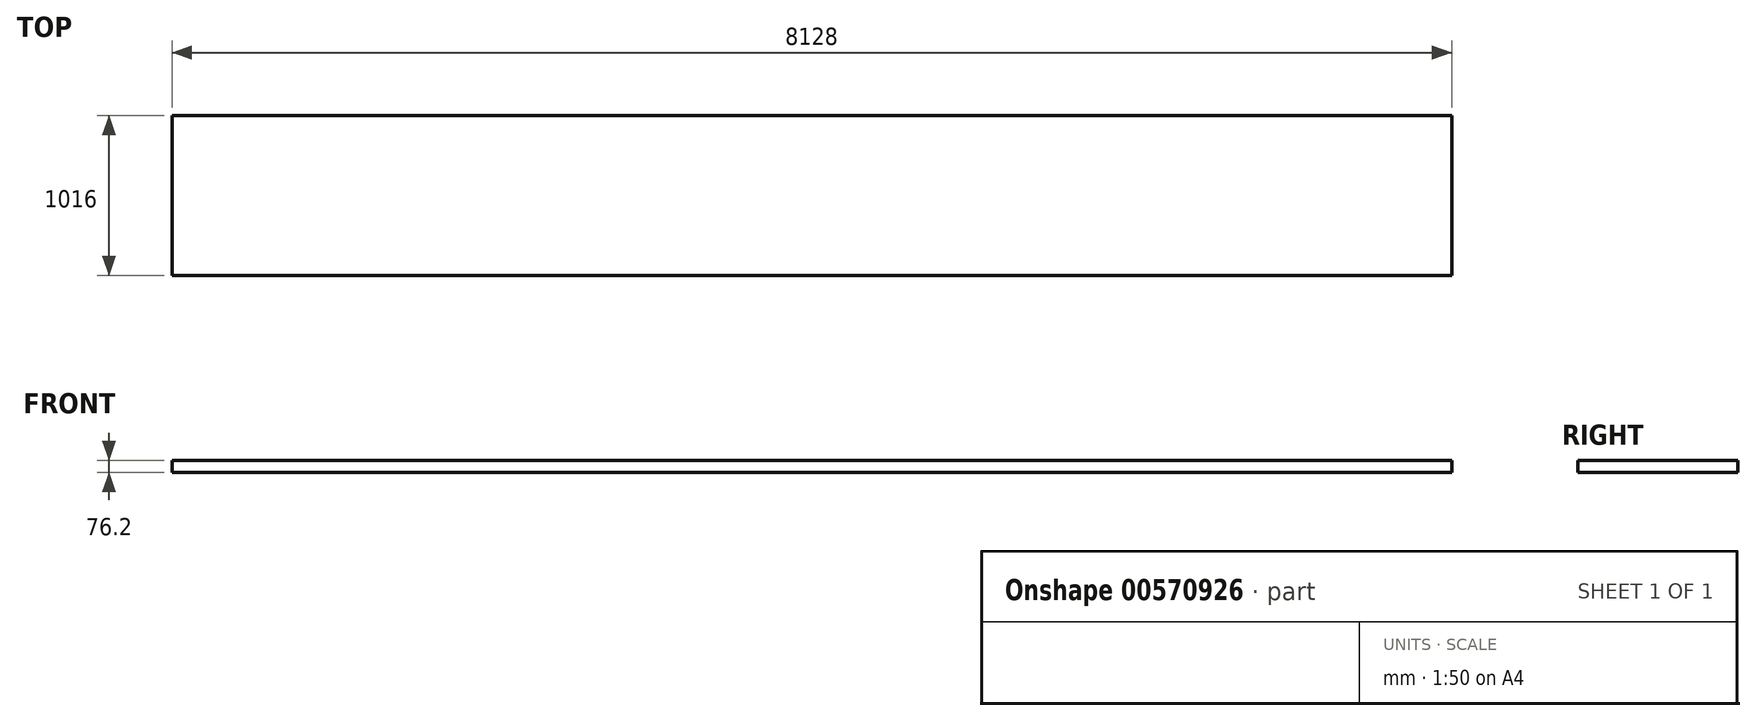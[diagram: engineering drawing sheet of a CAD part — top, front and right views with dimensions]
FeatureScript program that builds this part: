
annotation { "Feature Type Name" : "Feature", "Feature Type Description" : "" }
export const myFeature = defineFeature(function(context is Context, id is Id, definition is map)
    precondition{}
    {
        {
            var Q0;
            Q0=qCreatedBy(makeId("Top.planeOp"),FACE);
            var sketch = newSketch(context, id + "F0", { "sketchPlane" : qUnion([Q0])});
            skLineSegment(sketch, "E0.bottom", {"start": v(3361.46, -5509.04) * mm, "end": v(-4766.54, -5509.04) * mm});
            skLineSegment(sketch, "E0.top", {"start": v(3361.46, -6525.04) * mm, "end": v(-4766.54, -6525.04) * mm});
            skLineSegment(sketch, "E0.left", {"start": v(3361.46, -5509.04) * mm, "end": v(3361.46, -6525.04) * mm});
            skLineSegment(sketch, "E0.right", {"start": v(-4766.54, -5509.04) * mm, "end": v(-4766.54, -6525.04) * mm});
            skSolve(sketch);
        }
        {
            var Q0;
            Q0 = qSketchRegion(id + "F0", true);
            extrude(context, id + "F1", {"entities" : qUnion([Q0]), "depth" : 76.2 * mm, "offsetDistance" : 25.4 * mm});
        }
    });
